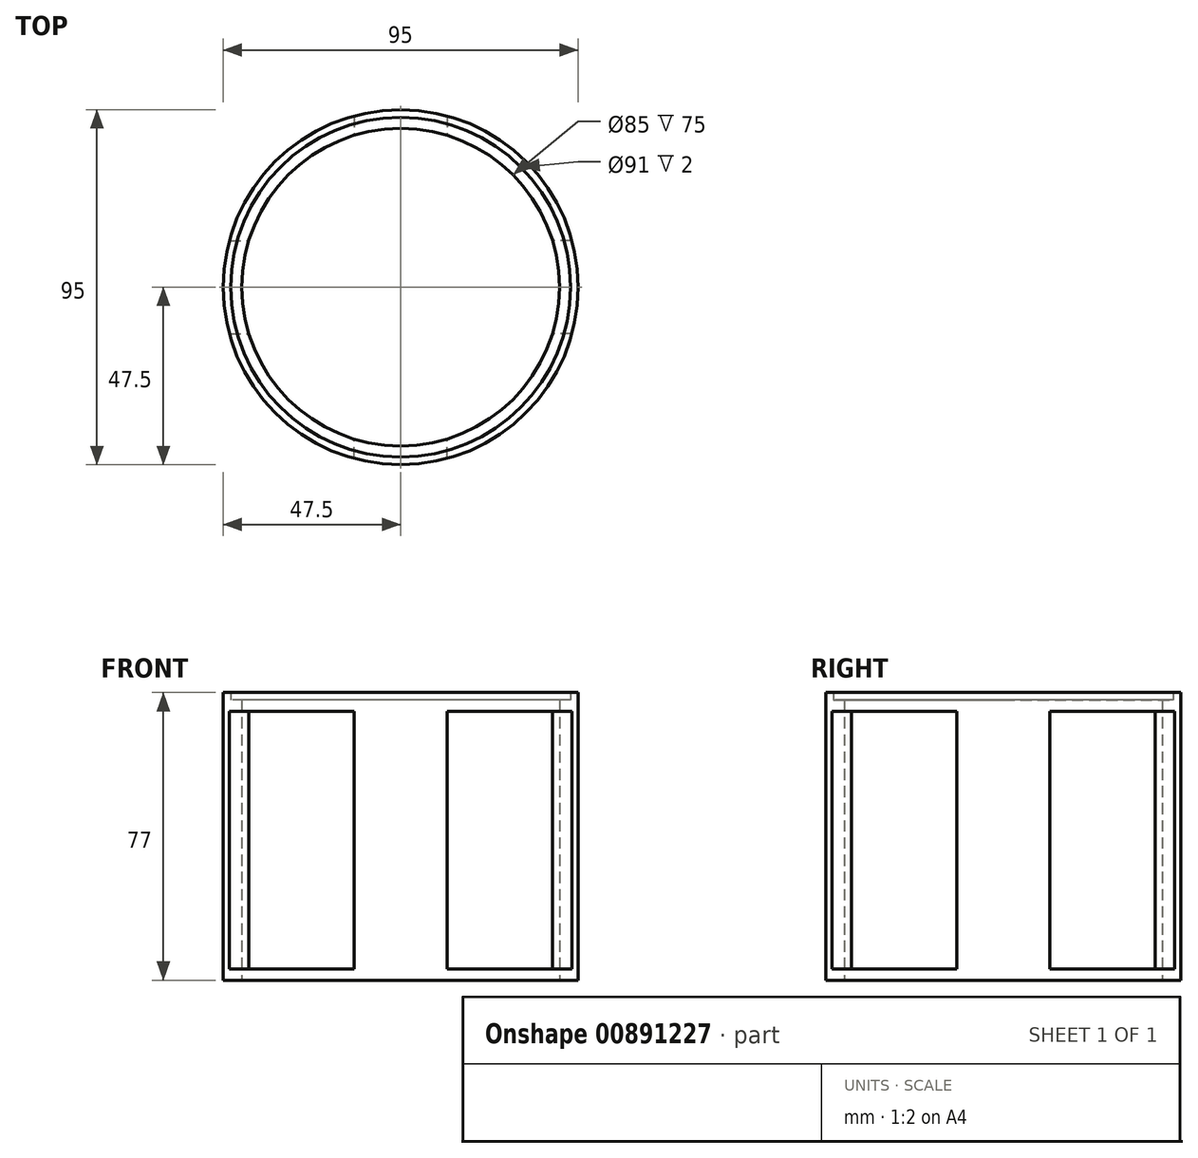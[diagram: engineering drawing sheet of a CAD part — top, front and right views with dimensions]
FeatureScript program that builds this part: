
annotation { "Feature Type Name" : "Feature", "Feature Type Description" : "" }
export const myFeature = defineFeature(function(context is Context, id is Id, definition is map)
    precondition{}
    {
        {
            var Q0;
            Q0=qCreatedBy(makeId("Top.planeOp"),FACE);
            var sketch = newSketch(context, id + "F0", { "sketchPlane" : qUnion([Q0])});
            skCircle(sketch, "E0", {"center": v(0, 0) * mm, "radius": 47.5 * mm});
            skCircle(sketch, "E1", {"center": v(0, 0) * mm, "radius": 42.5 * mm});
            skSolve(sketch);
        }
        {
            var Q0;
            Q0 = qSketchRegion(id + "F0", true);
            extrude(context, id + "F1", {"entities" : qUnion([Q0]), "depth" : 3 * mm, "offsetDistance" : 25 * mm});
        }
        {
            var Q0;
            Q0=qCreatedBy(makeId("Top.planeOp"),FACE);
            var sketch = newSketch(context, id + "F2", { "sketchPlane" : qUnion([Q0])});
            skArc(sketch, "E2.0", {"start": v(12.43, 45.84) * mm, "mid": v(0, 47.5) * mm, "end": v(-12.43, 45.84) * mm});
            skArc(sketch, "E3.0", {"start": v(-2.5, 42.43) * mm, "mid": v(-7.52, 41.83) * mm, "end": v(-12.43, 40.64) * mm});
            skArc(sketch, "E4", {"start": v(-12.43, 40.64) * mm, "mid": v(-6.29, 42.03) * mm, "end": v(0, 42.5) * mm});
            skLineSegment(sketch, "E5", {"start": v(-12.43, 40.64) * mm, "end": v(-12.43, 45.84) * mm});
            skArc(sketch, "E6.MirrorCS", {"start": v(2.5, 42.43) * mm, "mid": v(7.52, 41.83) * mm, "end": v(12.43, 40.64) * mm});
            skLineSegment(sketch, "E7.MirrorCS", {"start": v(12.43, 40.64) * mm, "end": v(12.43, 45.84) * mm});
            skArc(sketch, "E8.MirrorCS", {"start": v(12.43, 40.64) * mm, "mid": v(6.29, 42.03) * mm, "end": v(0, 42.5) * mm});
            skArc(sketch, "E9.1.0", {"start": v(-45.84, 12.43) * mm, "mid": v(-47.5, 0) * mm, "end": v(-45.84, -12.43) * mm});
            skArc(sketch, "E9.1.1", {"start": v(-42.43, 2.5) * mm, "mid": v(-41.83, 7.52) * mm, "end": v(-40.64, 12.43) * mm});
            skArc(sketch, "E9.1.2", {"start": v(-40.64, 12.43) * mm, "mid": v(-42.03, 6.29) * mm, "end": v(-42.5, 0) * mm});
            skLineSegment(sketch, "E9.1.3", {"start": v(-40.64, -12.43) * mm, "end": v(-45.84, -12.43) * mm});
            skArc(sketch, "E9.1.4", {"start": v(-40.64, -12.43) * mm, "mid": v(-42.03, -6.29) * mm, "end": v(-42.5, 0) * mm});
            skLineSegment(sketch, "E9.1.5", {"start": v(-40.64, 12.43) * mm, "end": v(-45.84, 12.43) * mm});
            skArc(sketch, "E9.1.6", {"start": v(-42.43, -2.5) * mm, "mid": v(-41.83, -7.52) * mm, "end": v(-40.64, -12.43) * mm});
            skArc(sketch, "E9.2.0", {"start": v(-12.43, -45.84) * mm, "mid": v(0, -47.5) * mm, "end": v(12.43, -45.84) * mm});
            skArc(sketch, "E9.2.1", {"start": v(-2.5, -42.43) * mm, "mid": v(-7.52, -41.83) * mm, "end": v(-12.43, -40.64) * mm});
            skArc(sketch, "E9.2.2", {"start": v(-12.43, -40.64) * mm, "mid": v(-6.29, -42.03) * mm, "end": v(0, -42.5) * mm});
            skLineSegment(sketch, "E9.2.3", {"start": v(12.43, -40.64) * mm, "end": v(12.43, -45.84) * mm});
            skArc(sketch, "E9.2.4", {"start": v(12.43, -40.64) * mm, "mid": v(6.29, -42.03) * mm, "end": v(0, -42.5) * mm});
            skLineSegment(sketch, "E9.2.5", {"start": v(-12.43, -40.64) * mm, "end": v(-12.43, -45.84) * mm});
            skArc(sketch, "E9.2.6", {"start": v(2.5, -42.43) * mm, "mid": v(7.52, -41.83) * mm, "end": v(12.43, -40.64) * mm});
            skArc(sketch, "E9.3.0", {"start": v(45.84, -12.43) * mm, "mid": v(47.5, 0) * mm, "end": v(45.84, 12.43) * mm});
            skArc(sketch, "E9.3.1", {"start": v(42.43, -2.5) * mm, "mid": v(41.83, -7.52) * mm, "end": v(40.64, -12.43) * mm});
            skArc(sketch, "E9.3.2", {"start": v(40.64, -12.43) * mm, "mid": v(42.03, -6.29) * mm, "end": v(42.5, 0) * mm});
            skLineSegment(sketch, "E9.3.3", {"start": v(40.64, 12.43) * mm, "end": v(45.84, 12.43) * mm});
            skArc(sketch, "E9.3.4", {"start": v(40.64, 12.43) * mm, "mid": v(42.03, 6.29) * mm, "end": v(42.5, 0) * mm});
            skLineSegment(sketch, "E9.3.5", {"start": v(40.64, -12.43) * mm, "end": v(45.84, -12.43) * mm});
            skArc(sketch, "E9.3.6", {"start": v(42.43, 2.5) * mm, "mid": v(41.83, 7.52) * mm, "end": v(40.64, 12.43) * mm});
            skSolve(sketch);
        }
        {
            var Q0;
            Q0 = qSketchRegion(id + "F2", true);
            extrude(context, id + "F3", {"entities" : qUnion([Q0]), "operationType" : NewBodyOperationType.ADD, "depth" : 72 * mm, "offsetDistance" : 25 * mm});
        }
        {
            var Q0;
            Q0=makeQuery(id+"F3.opExtrude","CAP_FACE",FACE,{"disambiguationData":[OSD([sQuery(id+"F2.wireOp",EDGE,"E9.1.0"),sQuery(id+"F2.wireOp",EDGE,"E9.1.2"),sQuery(id+"F2.wireOp",EDGE,"E9.1.3"),sQuery(id+"F2.wireOp",EDGE,"E9.1.4"),sQuery(id+"F2.wireOp",EDGE,"E9.1.5"),sQuery(id+"F2.wireOp",EDGE,"E9.1.6")])],"isStart":false});
            var sketch = newSketch(context, id + "F4", { "sketchPlane" : qUnion([Q0])});
            skCircle(sketch, "E10", {"center": v(0, 0) * mm, "radius": 47.5 * mm});
            skCircle(sketch, "E11", {"center": v(0, 0) * mm, "radius": 42.5 * mm});
            skSolve(sketch);
        }
        {
            var Q0;
            Q0 = qSketchRegion(id + "F4", true);
            extrude(context, id + "F5", {"entities" : qUnion([Q0]), "operationType" : NewBodyOperationType.ADD, "depth" : 3 * mm, "offsetDistance" : 25 * mm});
        }
        {
            var Q0;
            Q0=makeQuery(id+"F5.opExtrude","CAP_FACE",FACE,{"disambiguationData":[OSD([sQuery(id+"F4.wireOp",EDGE,"E10"),sQuery(id+"F4.wireOp",EDGE,"E11")])],"isStart":false});
            var sketch = newSketch(context, id + "F6", { "sketchPlane" : qUnion([Q0])});
            skCircle(sketch, "E12", {"center": v(0, 0) * mm, "radius": 45.5 * mm});
            skCircle(sketch, "E13", {"center": v(0, 0) * mm, "radius": 47.5 * mm});
            skSolve(sketch);
        }
        {
            var Q0;
            Q0 = qSketchRegion(id + "F6", true);
            extrude(context, id + "F7", {"entities" : qUnion([Q0]), "operationType" : NewBodyOperationType.ADD, "depth" : 2 * mm, "offsetDistance" : 25 * mm});
        }
    });
